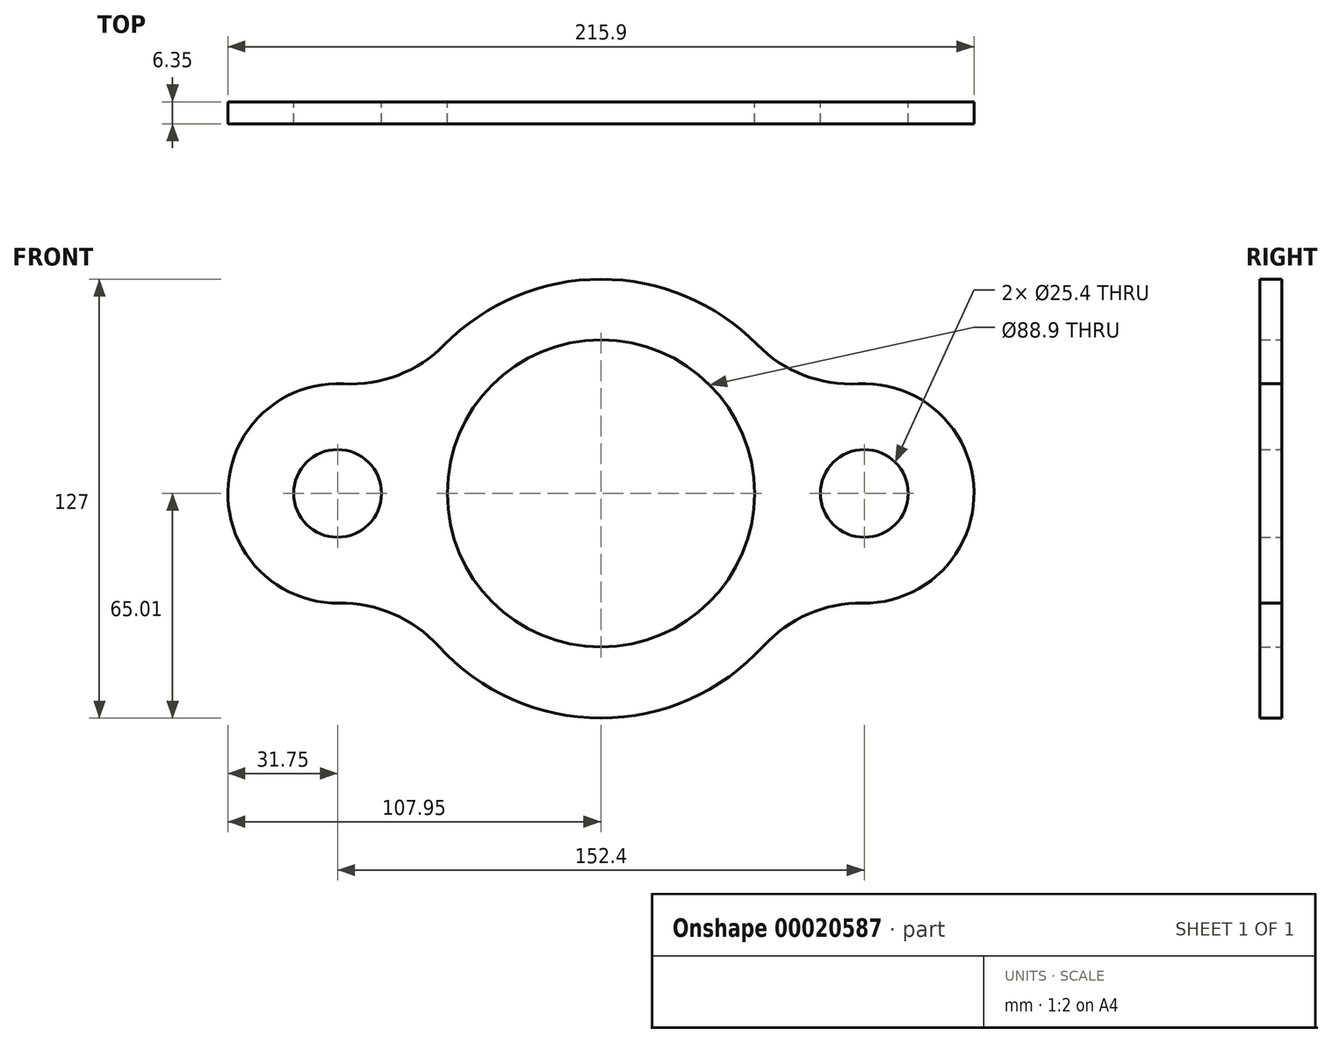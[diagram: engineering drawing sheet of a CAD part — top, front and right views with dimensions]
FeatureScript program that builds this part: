
annotation { "Feature Type Name" : "Feature", "Feature Type Description" : "" }
export const myFeature = defineFeature(function(context is Context, id is Id, definition is map)
    precondition{}
    {
        {
            var Q0;
            Q0=qCreatedBy(makeId("Front.planeOp"),FACE);
            var sketch = newSketch(context, id + "F0", { "sketchPlane" : qUnion([Q0])});
            skCircle(sketch, "E0", {"center": v(0, 0) * mm, "radius": 44.45 * mm});
            skArc(sketch, "E1", {"start": v(45.26, 43.02) * mm, "mid": v(0, 61.99) * mm, "end": v(-45.26, 43.02) * mm});
            skLineSegment(sketch, "E2", {"start": v(-63.48, 0) * mm, "end": v(-63.5, 0) * mm});
            skCircle(sketch, "E3", {"center": v(-76.2, 0) * mm, "radius": 12.7 * mm});
            skCircle(sketch, "E4", {"center": v(76.2, 0) * mm, "radius": 12.7 * mm});
            skArc(sketch, "E5", {"start": v(-74.48, 31.7) * mm, "mid": v(-107.94, 0.63) * mm, "end": v(-75.74, -31.75) * mm});
            skArc(sketch, "E6", {"start": v(75.74, -31.75) * mm, "mid": v(107.94, 0.63) * mm, "end": v(74.48, 31.7) * mm});
            skLineSegment(sketch, "E7.trimOffspring", {"start": v(63.48, 0) * mm, "end": v(63.5, 0) * mm});
            skArc(sketch, "E8.trimOffspring", {"start": v(-47, -44.22) * mm, "mid": v(0, -65.01) * mm, "end": v(47, -44.22) * mm});
            skPoint(sketch, "E9.visualSharp", {"position": v(-57.42, 25.6) * mm});
            skArc(sketch, "E9.filletArc", {"start": v(-74.48, 31.7) * mm, "mid": v(-58.65, 34.22) * mm, "end": v(-45.26, 43.02) * mm});
            skPoint(sketch, "E10.visualSharp", {"position": v(57.42, 25.6) * mm});
            skArc(sketch, "E10.filletArc", {"start": v(45.26, 43.02) * mm, "mid": v(58.65, 34.22) * mm, "end": v(74.48, 31.7) * mm});
            skPoint(sketch, "E11.visualSharp", {"position": v(-58.45, -26.33) * mm});
            skArc(sketch, "E11.filletArc", {"start": v(-47, -44.22) * mm, "mid": v(-60.03, -34.9) * mm, "end": v(-75.74, -31.75) * mm});
            skPoint(sketch, "E12.visualSharp", {"position": v(58.45, -26.33) * mm});
            skArc(sketch, "E12.filletArc", {"start": v(75.74, -31.75) * mm, "mid": v(60.03, -34.9) * mm, "end": v(47, -44.22) * mm});
            skSolve(sketch);
        }
        {
            var Q0;
            Q0=makeQuery(id+"F0.imprint","IMPRINT",FACE,{"disambiguationData":[TD([[makeQuery(id+"F0.imprint","IMPRINT",EDGE,{"derivedFrom":sQuery(id+"F0.wireOp",EDGE,"E0")}),-1.0]])]});
            extrude(context, id + "F1", {"entities" : qUnion([Q0]), "depth" : 6.35 * mm});
        }
    });
